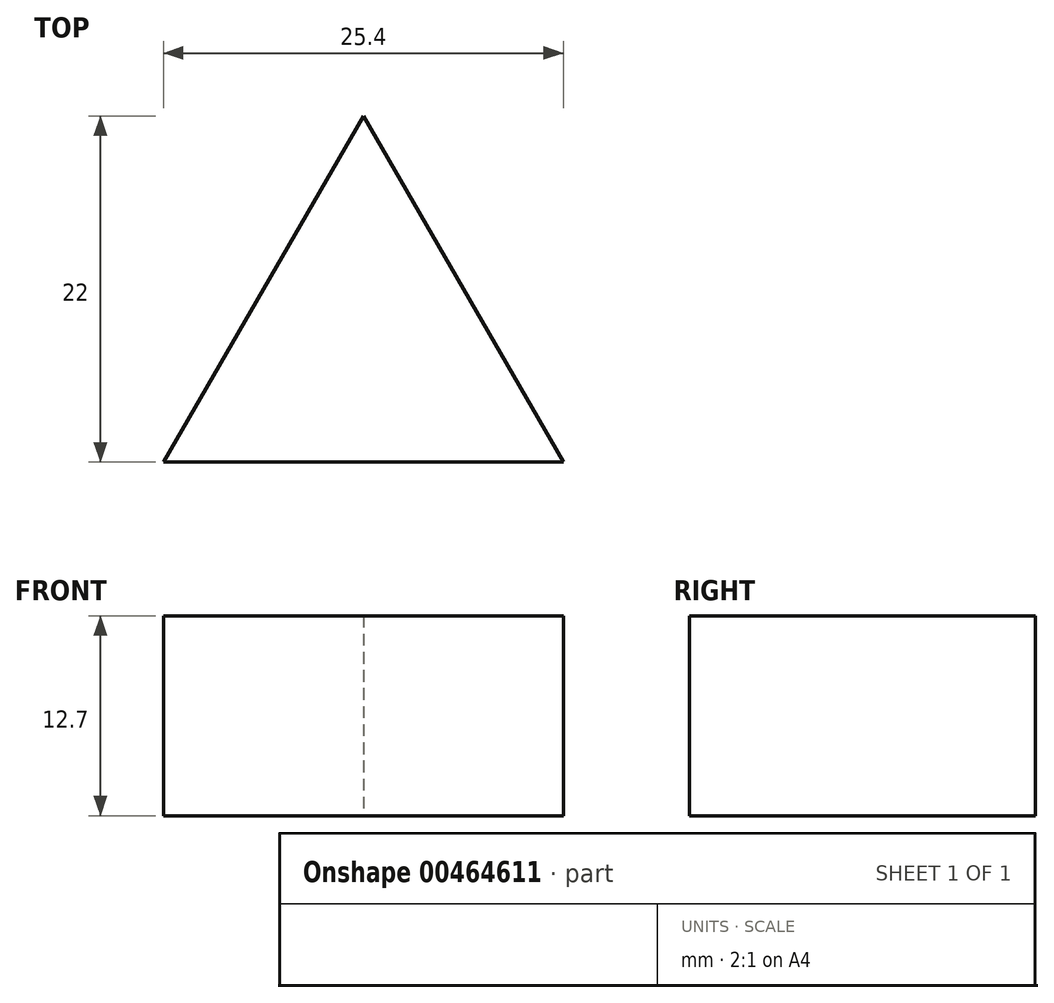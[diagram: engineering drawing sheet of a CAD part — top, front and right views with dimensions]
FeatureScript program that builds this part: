
annotation { "Feature Type Name" : "Feature", "Feature Type Description" : "" }
export const myFeature = defineFeature(function(context is Context, id is Id, definition is map)
    precondition{}
    {
        {
            var Q0;
            Q0=qCreatedBy(makeId("Top.planeOp"),FACE);
            var sketch = newSketch(context, id + "F0", { "sketchPlane" : qUnion([Q0])});
            skLineSegment(sketch, "E0", {"start": v(0, 9.14) * mm, "end": v(-12.7, -12.86) * mm});
            skLineSegment(sketch, "E1", {"start": v(-12.7, -12.86) * mm, "end": v(12.7, -12.86) * mm});
            skLineSegment(sketch, "E2", {"start": v(12.7, -12.86) * mm, "end": v(0, 9.14) * mm});
            skSolve(sketch);
        }
        {
            var Q0;
            Q0=makeQuery(id+"F0.imprint","IMPRINT",FACE,{"disambiguationData":[TD([[makeQuery(id+"F0.imprint","IMPRINT",EDGE,{"derivedFrom":sQuery(id+"F0.wireOp",EDGE,"E0")}),1.0]])]});
            extrude(context, id + "F1", {"entities" : qUnion([Q0]), "depth" : 12.7 * mm});
        }
    });
